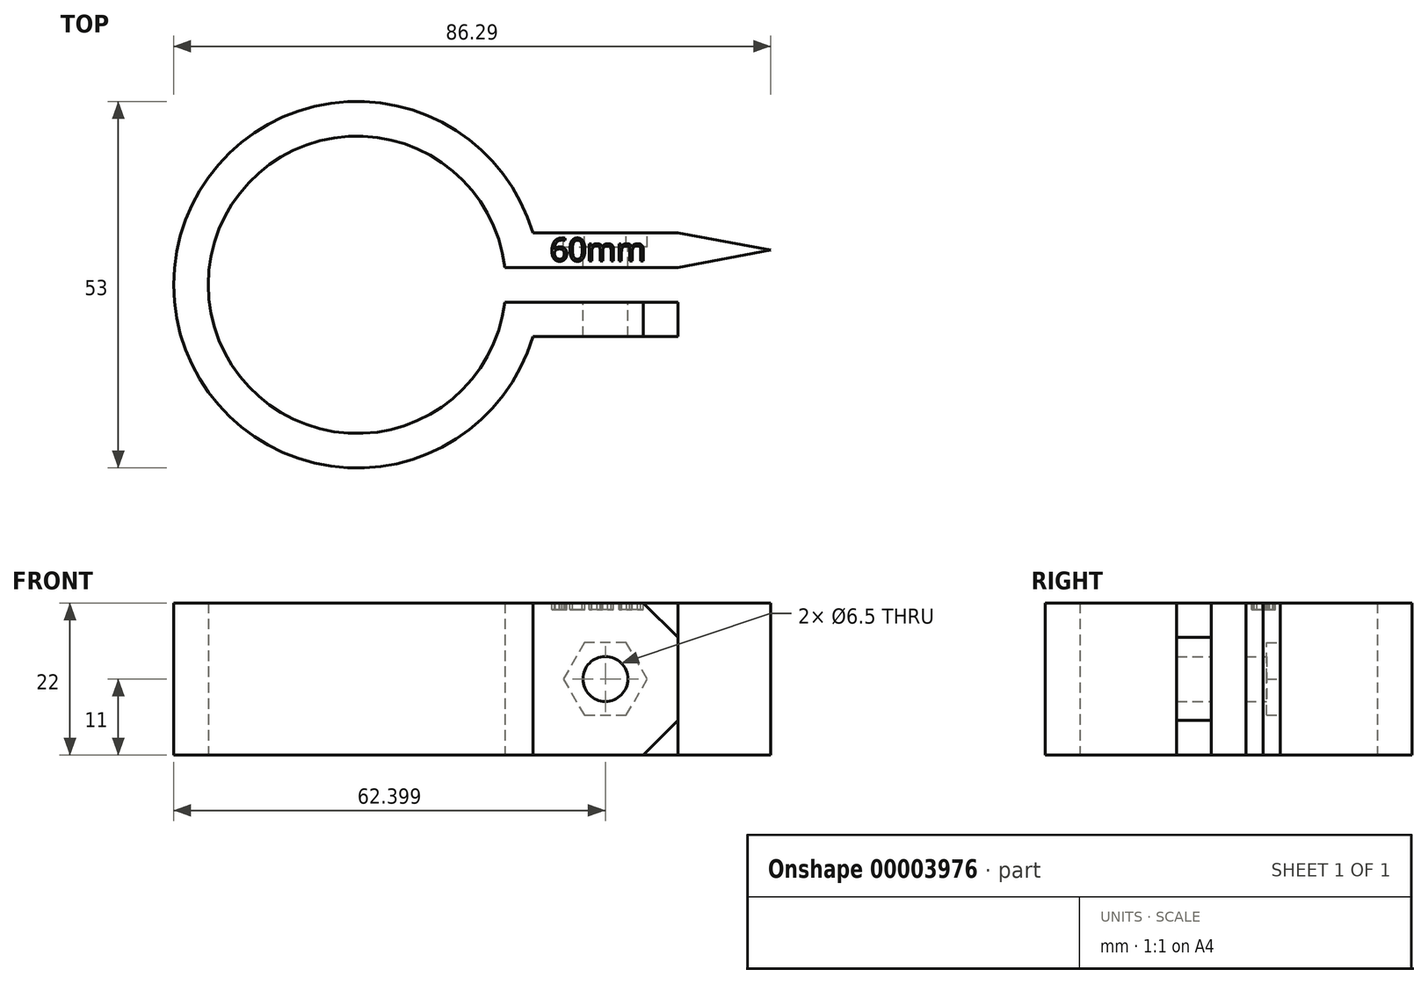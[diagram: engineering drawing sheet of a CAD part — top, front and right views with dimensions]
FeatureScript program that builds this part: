
annotation { "Feature Type Name" : "Feature", "Feature Type Description" : "" }
export const myFeature = defineFeature(function(context is Context, id is Id, definition is map)
    precondition{}
    {
        {
            var Q0;
            Q0=qCreatedBy(makeId("Top.planeOp"),FACE);
            var sketch = newSketch(context, id + "F0", { "sketchPlane" : qUnion([Q0])});
            skCircle(sketch, "E0", {"center": v(0, 0) * mm, "radius": 21.5 * mm});
            skCircle(sketch, "E1", {"center": v(0, 0) * mm, "radius": 26.5 * mm});
            skLineSegment(sketch, "E2", {"start": v(0, 0) * mm, "end": v(21.35, 2.5) * mm});
            skLineSegment(sketch, "E3.MirrorCS", {"start": v(0, 0) * mm, "end": v(21.35, -2.5) * mm});
            skLineSegment(sketch, "E4", {"start": v(21.35, 2.5) * mm, "end": v(46.38, 2.5) * mm});
            skLineSegment(sketch, "E5", {"start": v(46.38, 2.5) * mm, "end": v(46.38, 7.5) * mm});
            skLineSegment(sketch, "E6", {"start": v(46.38, 7.5) * mm, "end": v(25.42, 7.5) * mm});
            skLineSegment(sketch, "E7.MirrorCS", {"start": v(21.35, -2.5) * mm, "end": v(46.38, -2.5) * mm});
            skLineSegment(sketch, "E8.MirrorCS", {"start": v(46.38, -2.5) * mm, "end": v(46.38, -7.5) * mm});
            skLineSegment(sketch, "E9.MirrorCS", {"start": v(46.38, -7.5) * mm, "end": v(25.42, -7.5) * mm});
            skPoint(sketch, "E10", {"position": v(26.38, 2.5) * mm});
            skSolve(sketch);
        }
        {
            var Q0;
            {var subQ5=sQuery(id+"F0.wireOp",EDGE,"E2");var subQ7=sQuery(id+"F0.wireOp",EDGE,"E0");var subQ8=makeQuery(id+"F0.imprint","INTERSECT",VERTEX,{"derivedFrom":[subQ7,subQ5]});Q0=makeQuery(id+"F0.imprint","IMPRINT",FACE,{"disambiguationData":[TD([[makeQuery(id+"F0.imprint","IMPRINT",EDGE,{"disambiguationData":[TD([[subQ8,-1.0]])],"derivedFrom":subQ7}),-1.0]])]});}
            var Q1;
            {var subQ0=sQuery(id+"F0.wireOp",EDGE,"E4");Q1=makeQuery(id+"F0.imprint","IMPRINT",FACE,{"disambiguationData":[TD([[makeQuery(id+"F0.imprint","IMPRINT",EDGE,{"derivedFrom":subQ0}),1.0]])]});}
            var Q2;
            {var subQ0=sQuery(id+"F0.wireOp",EDGE,"E7.MirrorCS");Q2=makeQuery(id+"F0.imprint","IMPRINT",FACE,{"disambiguationData":[TD([[makeQuery(id+"F0.imprint","IMPRINT",EDGE,{"derivedFrom":subQ0}),-1.0]])]});}
            extrude(context, id + "F1", {"entities" : qUnion([Q0, Q1, Q2]), "depth" : 22 * mm});
        }
        {
            var Q0;
            Q0=makeQuery(id+"F1.opExtrude","SWEPT_FACE",FACE,{"disambiguationData":[OSD([sQuery(id+"F0.wireOp",EDGE,"E9.MirrorCS")])]});
            var sketch = newSketch(context, id + "F2", { "sketchPlane" : qUnion([Q0])});
            skLineSegment(sketch, "E11", {"start": v(35.9, 0) * mm, "end": v(35.9, 22) * mm, "construction": true});
            skPoint(sketch, "E12", {"position": v(35.9, 11) * mm});
            skSolve(sketch);
        }
        {
            var Q0;
            Q0=sQuery(id+"F2.wireOp",VERTEX,"E12");
            var Q1;
            Q1=makeQuery(id+"F1.opExtrude","SWEPT_BODY",BODY,{"disambiguationData":[OSD([sQuery(id+"F0.wireOp",EDGE,"E0"),sQuery(id+"F0.wireOp",EDGE,"E1"),sQuery(id+"F0.wireOp",EDGE,"E4"),sQuery(id+"F0.wireOp",EDGE,"E5"),sQuery(id+"F0.wireOp",EDGE,"E6"),sQuery(id+"F0.wireOp",EDGE,"E7.MirrorCS"),sQuery(id+"F0.wireOp",EDGE,"E8.MirrorCS"),sQuery(id+"F0.wireOp",EDGE,"E9.MirrorCS")])]});
            hole(context, id + "F3", {"style" : HoleStyle.SIMPLE, "endStyle" : HoleEndStyle.THROUGH, "holeDiameter" : 6.5 * mm, "tappedDepth" : 7 * mm, "tapClearance" : 3, "locations" : qUnion([Q0]), "scope" : qUnion([Q1]), "startStyle" : HoleStartStyle.PART});
        }
        {
            var Q0;
            Q0=makeQuery(id+"F1.opExtrude","CAP_FACE",FACE,{"disambiguationData":[OSD([sQuery(id+"F0.wireOp",EDGE,"E0"),sQuery(id+"F0.wireOp",EDGE,"E1"),sQuery(id+"F0.wireOp",EDGE,"E4"),sQuery(id+"F0.wireOp",EDGE,"E5"),sQuery(id+"F0.wireOp",EDGE,"E6"),sQuery(id+"F0.wireOp",EDGE,"E7.MirrorCS"),sQuery(id+"F0.wireOp",EDGE,"E8.MirrorCS"),sQuery(id+"F0.wireOp",EDGE,"E9.MirrorCS")])],"isStart":false});
            var sketch = newSketch(context, id + "F4", { "sketchPlane" : qUnion([Q0])});
            skLineSegment(sketch, "E13", {"start": v(46.38, 7.5) * mm, "end": v(59.8, 5) * mm});
            skPoint(sketch, "E13.endSnap0", {"position": v(46.38, 5) * mm});
            skLineSegment(sketch, "E14", {"start": v(59.8, 5) * mm, "end": v(46.38, 2.5) * mm});
            skSolve(sketch);
        }
        {
            var Q0;
            Q0=makeQuery(id+"F4.imprint","IMPRINT",FACE,{"disambiguationData":[TD([[makeQuery(id+"F4.imprint","IMPRINT",EDGE,{"derivedFrom":sQuery(id+"F4.wireOp",EDGE,"E13")}),-1.0]])]});
            var Q1;
            Q1=makeQuery(id+"F1.opExtrude","CAP_FACE",FACE,{"disambiguationData":[OSD([sQuery(id+"F0.wireOp",EDGE,"E0"),sQuery(id+"F0.wireOp",EDGE,"E1"),sQuery(id+"F0.wireOp",EDGE,"E4"),sQuery(id+"F0.wireOp",EDGE,"E5"),sQuery(id+"F0.wireOp",EDGE,"E6"),sQuery(id+"F0.wireOp",EDGE,"E7.MirrorCS"),sQuery(id+"F0.wireOp",EDGE,"E8.MirrorCS"),sQuery(id+"F0.wireOp",EDGE,"E9.MirrorCS")])],"isStart":true});
            extrude(context, id + "F5", {"entities" : qUnion([Q0]), "operationType" : NewBodyOperationType.ADD, "endBound" : BoundingType.UP_TO_SURFACE, "oppositeDirection" : true, "endBoundEntityFace" : qUnion([Q1]), "depth" : 25 * mm});
        }
        {
            var Q0;
            {var subQ0=sQuery(id+"F0.wireOp",EDGE,"E5");Q0=makeQuery(id+"F5.boolean.opBoolean","MERGE",FACE,{"derivedFrom":[makeQuery(id+"F1.opExtrude","CAP_FACE",FACE,{"disambiguationData":[OSD([sQuery(id+"F0.wireOp",EDGE,"E0"),sQuery(id+"F0.wireOp",EDGE,"E1"),sQuery(id+"F0.wireOp",EDGE,"E4"),subQ0,sQuery(id+"F0.wireOp",EDGE,"E6"),sQuery(id+"F0.wireOp",EDGE,"E7.MirrorCS"),sQuery(id+"F0.wireOp",EDGE,"E8.MirrorCS"),sQuery(id+"F0.wireOp",EDGE,"E9.MirrorCS")])],"isStart":false}),makeQuery(id+"F5.opExtrude","CAP_FACE",FACE,{"disambiguationData":[OSD([subQ0,sQuery(id+"F4.wireOp",EDGE,"E13"),sQuery(id+"F4.wireOp",EDGE,"E14")])],"isStart":true})]});}
            var sketch = newSketch(context, id + "F6", { "sketchPlane" : qUnion([Q0])});
            skText(sketch, "E15", { "text": "60mm", "fontName": "OpenSans-Regular.ttf"});
            const initialGuessF6  = {"E15": [0.0279, 0.00343, 1, 0, 0.00332]};
            skSetInitialGuess(sketch, initialGuessF6);
            skSolve(sketch);
        }
        {
            var Q0;
            Q0 = qSketchRegion(id + "F6", true);
            extrude(context, id + "F7", {"entities" : qUnion([Q0]), "operationType" : NewBodyOperationType.REMOVE, "oppositeDirection" : true, "depth" : 1 * mm});
        }
        {
            var Q0;
            Q0=makeQuery(id+"F1.opExtrude","SWEPT_FACE",FACE,{"disambiguationData":[OSD([sQuery(id+"F0.wireOp",EDGE,"E6")])]});
            var sketch = newSketch(context, id + "F8", { "sketchPlane" : qUnion([Q0])});
            skCircle(sketch, "E16.cCircle", {"center": v(-35.9, 11) * mm, "radius": 5.25 * mm, "construction": true});
            skLineSegment(sketch, "E16.0", {"start": v(-41.96, 11) * mm, "end": v(-38.93, 16.25) * mm});
            skLineSegment(sketch, "E16.1", {"start": v(-38.93, 16.25) * mm, "end": v(-32.87, 16.25) * mm});
            skLineSegment(sketch, "E16.2", {"start": v(-32.87, 16.25) * mm, "end": v(-29.84, 11) * mm});
            skLineSegment(sketch, "E16.3", {"start": v(-29.84, 11) * mm, "end": v(-32.87, 5.75) * mm});
            skLineSegment(sketch, "E16.4", {"start": v(-32.87, 5.75) * mm, "end": v(-38.93, 5.75) * mm});
            skLineSegment(sketch, "E16.5", {"start": v(-38.93, 5.75) * mm, "end": v(-41.96, 11) * mm});
            skPoint(sketch, "E16.0.midPoint", {"position": v(-40.45, 13.63) * mm});
            skSolve(sketch);
        }
        {
            var Q0;
            Q0=makeQuery(id+"F8.imprint","IMPRINT",FACE,{"disambiguationData":[TD([[makeQuery(id+"F8.imprint","IMPRINT",EDGE,{"derivedFrom":sQuery(id+"F8.wireOp",EDGE,"E16.0")}),-1.0]])]});
            extrude(context, id + "F9", {"entities" : qUnion([Q0]), "operationType" : NewBodyOperationType.REMOVE, "oppositeDirection" : true, "depth" : 2 * mm});
        }
        {
            var Q0;
            Q0=makeQuery(id+"F1.opExtrude","CAP_EDGE",EDGE,{"disambiguationData":[OSD([sQuery(id+"F0.wireOp",EDGE,"E8.MirrorCS")])],"isStart":false});
            var Q1;
            Q1=makeQuery(id+"F1.opExtrude","CAP_EDGE",EDGE,{"disambiguationData":[OSD([sQuery(id+"F0.wireOp",EDGE,"E8.MirrorCS")])],"isStart":true});
            chamfer(context, id + "F10", {"entities" : qUnion([Q0, Q1]), "width" : 5 * mm, "tangentPropagation" : true});
        }
    });
